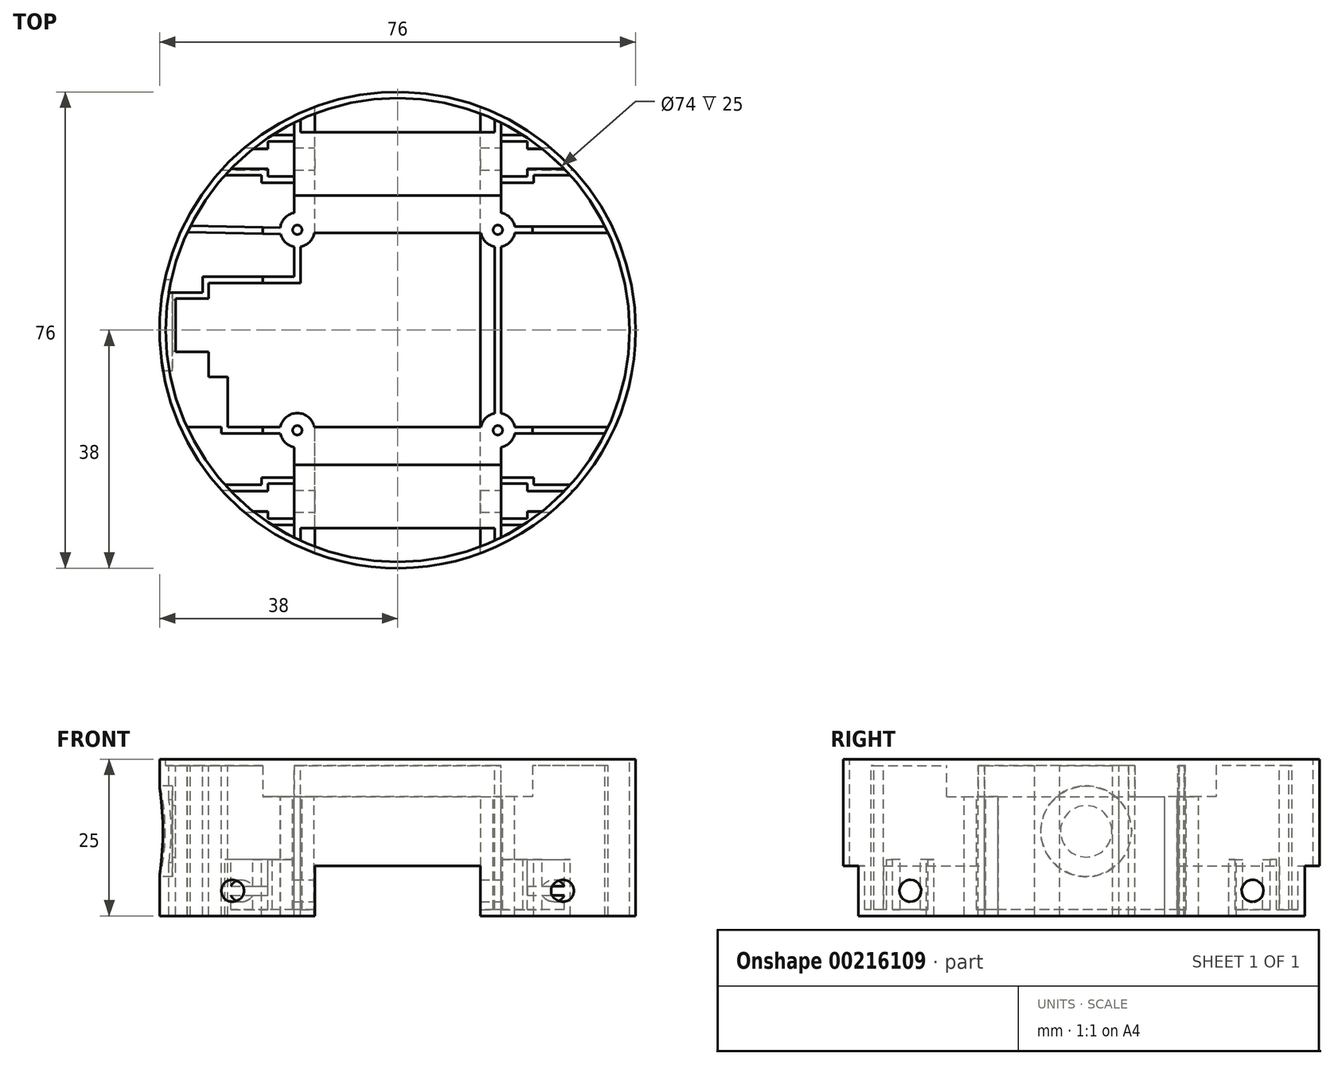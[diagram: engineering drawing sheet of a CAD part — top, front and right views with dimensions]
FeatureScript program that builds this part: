
annotation { "Feature Type Name" : "Feature", "Feature Type Description" : "" }
export const myFeature = defineFeature(function(context is Context, id is Id, definition is map)
    precondition{}
    {
        {
            var Q0;
            Q0=qCreatedBy(makeId("Top.planeOp"),FACE);
            var sketch = newSketch(context, id + "F0", { "sketchPlane" : qUnion([Q0])});
            skCircle(sketch, "E0", {"center": v(0, 0) * mm, "radius": 38 * mm});
            skLineSegment(sketch, "E1", {"start": v(-13, 35.7) * mm, "end": v(-13, -35.7) * mm, "construction": true});
            skLineSegment(sketch, "E2", {"start": v(13, 35.7) * mm, "end": v(13, -35.7) * mm, "construction": true});
            skLineSegment(sketch, "E3", {"start": v(0, 38) * mm, "end": v(0, -38) * mm, "construction": true});
            skSolve(sketch);
        }
        {
            var Q0;
            Q0=makeQuery(id+"F0.imprint","IMPRINT",FACE,{"disambiguationData":[TD([[makeQuery(id+"F0.imprint","IMPRINT",EDGE,{"derivedFrom":sQuery(id+"F0.wireOp",EDGE,"E0")}),1.0]])]});
            extrude(context, id + "F1", {"entities" : qUnion([Q0]), "depth" : 25 * mm});
        }
        {
            var Q0;
            Q0=makeQuery(id+"F1.opExtrude","CAP_FACE",FACE,{"disambiguationData":[OSD([sQuery(id+"F0.wireOp",EDGE,"E0")])],"isStart":false});
            var sketch = newSketch(context, id + "F2", { "sketchPlane" : qUnion([Q0])});
            skCircle(sketch, "E4", {"center": v(0, 0) * mm, "radius": 37 * mm});
            skLineSegment(sketch, "E5", {"start": v(-36.66, 5) * mm, "end": v(-30.14, 5) * mm});
            skLineSegment(sketch, "E6", {"start": v(-30.14, 5) * mm, "end": v(-30.14, 7.5) * mm});
            skLineSegment(sketch, "E7", {"start": v(-30.14, 7.5) * mm, "end": v(-27.14, 7.5) * mm});
            skLineSegment(sketch, "E8", {"start": v(-27.14, -7.5) * mm, "end": v(-30.14, -7.5) * mm});
            skLineSegment(sketch, "E9", {"start": v(-30.14, -7.5) * mm, "end": v(-30.14, -3.5) * mm});
            skLineSegment(sketch, "E10", {"start": v(-30.14, -3.5) * mm, "end": v(-36.83, -3.5) * mm});
            skLineSegment(sketch, "E11", {"start": v(0, 0) * mm, "end": v(-9.8, 0) * mm, "construction": true});
            skLineSegment(sketch, "E12", {"start": v(-27.14, -7.5) * mm, "end": v(-27.14, -15.5) * mm});
            skLineSegment(sketch, "E13", {"start": v(-35.44, 5) * mm, "end": v(-35.44, -3.5) * mm});
            skLineSegment(sketch, "E14", {"start": v(-36.51, 6) * mm, "end": v(-31.14, 6) * mm});
            skLineSegment(sketch, "E15", {"start": v(-31.14, 6) * mm, "end": v(-31.14, 8.5) * mm});
            skLineSegment(sketch, "E16", {"start": v(-31.14, 8.5) * mm, "end": v(-16.5, 8.5) * mm});
            skLineSegment(sketch, "E17", {"start": v(-21.04, -16.5) * mm, "end": v(-28.14, -16.5) * mm});
            skLineSegment(sketch, "E18", {"start": v(-28.14, -16.5) * mm, "end": v(-28.14, -8.5) * mm});
            skLineSegment(sketch, "E19", {"start": v(-28.14, -8.5) * mm, "end": v(-31.14, -8.5) * mm});
            skLineSegment(sketch, "E20", {"start": v(-31.14, -8.5) * mm, "end": v(-31.14, -4.5) * mm});
            skLineSegment(sketch, "E21", {"start": v(-31.14, -4.5) * mm, "end": v(-36.73, -4.5) * mm});
            skLineSegment(sketch, "E22", {"start": v(-33.49, -3.5) * mm, "end": v(-33.49, -4.5) * mm, "construction": true});
            skLineSegment(sketch, "E23", {"start": v(-30.14, -5.17) * mm, "end": v(-31.14, -5.17) * mm, "construction": true});
            skLineSegment(sketch, "E24", {"start": v(-29.18, -7.5) * mm, "end": v(-29.18, -8.5) * mm, "construction": true});
            skLineSegment(sketch, "E25", {"start": v(-28.14, -9.88) * mm, "end": v(-27.14, -9.88) * mm, "construction": true});
            skLineSegment(sketch, "E26", {"start": v(-23.9, -15.5) * mm, "end": v(-23.9, -16.5) * mm, "construction": true});
            skLineSegment(sketch, "E27", {"start": v(-9.14, -7.14) * mm, "end": v(-8.14, -7.14) * mm, "construction": true});
            skLineSegment(sketch, "E28", {"start": v(-20.62, 8.5) * mm, "end": v(-20.62, 7.5) * mm, "construction": true});
            skLineSegment(sketch, "E29", {"start": v(-32.73, 6) * mm, "end": v(-32.73, 5) * mm, "construction": true});
            skLineSegment(sketch, "E30", {"start": v(-31.14, 6.96) * mm, "end": v(-30.14, 6.96) * mm, "construction": true});
            skLineSegment(sketch, "E31.bottom", {"start": v(-16, 16) * mm, "end": v(16, 16) * mm, "construction": true});
            skLineSegment(sketch, "E31.top", {"start": v(-16, -16) * mm, "end": v(16, -16) * mm, "construction": true});
            skLineSegment(sketch, "E31.left", {"start": v(-16, 16) * mm, "end": v(-16, -16) * mm, "construction": true});
            skLineSegment(sketch, "E31.right", {"start": v(16, 16) * mm, "end": v(16, -16) * mm, "construction": true});
            skLineSegment(sketch, "E32", {"start": v(0, 0) * mm, "end": v(0, 2.04) * mm, "construction": true});
            skCircle(sketch, "E33", {"center": v(-16, 16) * mm, "radius": 0.75 * mm});
            skCircle(sketch, "E34", {"center": v(16, 16) * mm, "radius": 0.75 * mm});
            skCircle(sketch, "E35", {"center": v(16, -16) * mm, "radius": 0.75 * mm});
            skCircle(sketch, "E36", {"center": v(-16, -16) * mm, "radius": 0.75 * mm});
            skCircle(sketch, "E37", {"center": v(-16, 16) * mm, "radius": 2.75 * mm});
            skCircle(sketch, "E38", {"center": v(16, 16) * mm, "radius": 2.75 * mm});
            skCircle(sketch, "E39", {"center": v(-16, -16) * mm, "radius": 2.75 * mm});
            skCircle(sketch, "E40", {"center": v(16, -16) * mm, "radius": 2.75 * mm});
            skLineSegment(sketch, "E41", {"start": v(-16, 16.75) * mm, "end": v(-16, 18.75) * mm, "construction": true});
            skLineSegment(sketch, "E42", {"start": v(-16.5, 18.7) * mm, "end": v(-16.5, 33.12) * mm});
            skLineSegment(sketch, "E43", {"start": v(-16.5, 33.12) * mm, "end": v(-15.5, 33.6) * mm});
            skLineSegment(sketch, "E44", {"start": v(-15.5, 33.6) * mm, "end": v(-15.5, 18.7) * mm});
            skLineSegment(sketch, "E45", {"start": v(15.5, 18.7) * mm, "end": v(15.5, 33.6) * mm});
            skLineSegment(sketch, "E46", {"start": v(16.5, 18.7) * mm, "end": v(16.5, 33.12) * mm});
            skLineSegment(sketch, "E47", {"start": v(-18.73, 16.34) * mm, "end": v(-33.05, 16.63) * mm});
            skLineSegment(sketch, "E48", {"start": v(-18.67, 15.34) * mm, "end": v(-33.53, 15.63) * mm});
            skLineSegment(sketch, "E49", {"start": v(18.7, 16.5) * mm, "end": v(33.12, 16.5) * mm});
            skLineSegment(sketch, "E50", {"start": v(18.7, 15.5) * mm, "end": v(33.6, 15.5) * mm});
            skLineSegment(sketch, "E51", {"start": v(-18.7, -16.5) * mm, "end": v(-33.12, -16.5) * mm});
            skLineSegment(sketch, "E52", {"start": v(-18.7, -15.5) * mm, "end": v(-33.6, -15.5) * mm});
            skLineSegment(sketch, "E53", {"start": v(-16.5, -18.7) * mm, "end": v(-16.5, -33.12) * mm});
            skLineSegment(sketch, "E54", {"start": v(-15.5, -18.7) * mm, "end": v(-15.5, -33.6) * mm});
            skLineSegment(sketch, "E55", {"start": v(15.5, -18.7) * mm, "end": v(15.5, -33.6) * mm});
            skLineSegment(sketch, "E56", {"start": v(16.5, -18.7) * mm, "end": v(16.5, -33.12) * mm});
            skLineSegment(sketch, "E57", {"start": v(18.7, -15.5) * mm, "end": v(33.6, -15.5) * mm});
            skLineSegment(sketch, "E58", {"start": v(18.7, -16.5) * mm, "end": v(33.12, -16.5) * mm});
            skLineSegment(sketch, "E59", {"start": v(-13.3, 16.5) * mm, "end": v(13.3, 16.5) * mm});
            skLineSegment(sketch, "E60", {"start": v(-13.3, 15.5) * mm, "end": v(13.3, 15.5) * mm});
            skLineSegment(sketch, "E61", {"start": v(-16.5, 13.3) * mm, "end": v(-16.5, 8.5) * mm});
            skLineSegment(sketch, "E62", {"start": v(-15.5, 13.3) * mm, "end": v(-15.5, 8.5) * mm});
            skLineSegment(sketch, "E63", {"start": v(15.5, 13.3) * mm, "end": v(15.5, -13.3) * mm});
            skLineSegment(sketch, "E64", {"start": v(16.5, 13.3) * mm, "end": v(16.5, -13.3) * mm});
            skLineSegment(sketch, "E65", {"start": v(-13.3, -15.5) * mm, "end": v(13.3, -15.5) * mm});
            skLineSegment(sketch, "E66", {"start": v(-13.3, -16.5) * mm, "end": v(13.3, -16.5) * mm});
            skLineSegment(sketch, "E67", {"start": v(-25.45, -15.5) * mm, "end": v(-25.45, -16.5) * mm, "construction": true});
            skLineSegment(sketch, "E68", {"start": v(-16.5, -22.64) * mm, "end": v(-15.5, -22.64) * mm, "construction": true});
            skLineSegment(sketch, "E69", {"start": v(5.35, -15.5) * mm, "end": v(5.35, -16.5) * mm, "construction": true});
            skLineSegment(sketch, "E70", {"start": v(15.5, -24.3) * mm, "end": v(16.5, -24.3) * mm, "construction": true});
            skLineSegment(sketch, "E71", {"start": v(23.19, -15.5) * mm, "end": v(23.19, -16.5) * mm, "construction": true});
            skLineSegment(sketch, "E72", {"start": v(15.5, -9.1) * mm, "end": v(16.5, -9.1) * mm, "construction": true});
            skLineSegment(sketch, "E73", {"start": v(27.17, 16.5) * mm, "end": v(27.17, 15.5) * mm, "construction": true});
            skLineSegment(sketch, "E74", {"start": v(15.5, 26.6) * mm, "end": v(16.5, 26.6) * mm, "construction": true});
            skLineSegment(sketch, "E75", {"start": v(-15.5, 26.15) * mm, "end": v(-16.5, 26.15) * mm, "construction": true});
            skLineSegment(sketch, "E76", {"start": v(-25.9, 16.48) * mm, "end": v(-25.91, 15.48) * mm, "construction": true});
            skLineSegment(sketch, "E77", {"start": v(-15.5, 10.06) * mm, "end": v(-16.5, 10.06) * mm, "construction": true});
            skLineSegment(sketch, "E78", {"start": v(-3.42, 16.5) * mm, "end": v(-3.42, 15.5) * mm, "construction": true});
            skLineSegment(sketch, "E79.bottom", {"start": v(-16.5, 30.12) * mm, "end": v(-20.7, 30.12) * mm});
            skLineSegment(sketch, "E79.top", {"start": v(-16.5, 24.52) * mm, "end": v(-20.7, 24.52) * mm});
            skLineSegment(sketch, "E79.left", {"start": v(-16.5, 30.12) * mm, "end": v(-16.5, 24.52) * mm});
            skLineSegment(sketch, "E79.right", {"start": v(-20.7, 30.12) * mm, "end": v(-20.7, 24.52) * mm});
            skLineSegment(sketch, "E80", {"start": v(-20.7, 28.92) * mm, "end": v(-23.08, 28.92) * mm});
            skLineSegment(sketch, "E81", {"start": v(-26.6, 25.72) * mm, "end": v(-20.7, 25.72) * mm});
            skLineSegment(sketch, "E82", {"start": v(-16.5, 27.32) * mm, "end": v(-24.96, 27.32) * mm, "construction": true});
            skLineSegment(sketch, "E83", {"start": v(-16.5, 31.12) * mm, "end": v(-20.02, 31.12) * mm});
            skLineSegment(sketch, "E84", {"start": v(-27.53, 24.72) * mm, "end": v(-21.7, 24.72) * mm});
            skLineSegment(sketch, "E85", {"start": v(-21.7, 24.72) * mm, "end": v(-21.7, 23.52) * mm});
            skLineSegment(sketch, "E86", {"start": v(-21.7, 23.52) * mm, "end": v(-16.5, 23.52) * mm});
            skLineSegment(sketch, "E87", {"start": v(-18.26, 31.12) * mm, "end": v(-18.26, 30.12) * mm, "construction": true});
            skLineSegment(sketch, "E88", {"start": v(-25.05, 24.72) * mm, "end": v(-25.05, 25.72) * mm, "construction": true});
            skLineSegment(sketch, "E89", {"start": v(-21.7, 24.52) * mm, "end": v(-20.7, 24.52) * mm, "construction": true});
            skLineSegment(sketch, "E90", {"start": v(-17.39, 24.52) * mm, "end": v(-17.39, 23.52) * mm, "construction": true});
            skPoint(sketch, "E90.endSnap0", {"position": v(-19.1, 23.52) * mm});
            skLineSegment(sketch, "E91.MirrorCS", {"start": v(16.5, 31.12) * mm, "end": v(20.02, 31.12) * mm});
            skLineSegment(sketch, "E92.MirrorCS", {"start": v(16.5, 30.12) * mm, "end": v(20.7, 30.12) * mm});
            skLineSegment(sketch, "E93.MirrorCS", {"start": v(20.7, 28.92) * mm, "end": v(23.08, 28.92) * mm});
            skLineSegment(sketch, "E94.MirrorCS", {"start": v(20.7, 30.12) * mm, "end": v(20.7, 24.52) * mm});
            skLineSegment(sketch, "E95.MirrorCS", {"start": v(16.5, 24.52) * mm, "end": v(20.7, 24.52) * mm});
            skLineSegment(sketch, "E96.MirrorCS", {"start": v(21.7, 23.52) * mm, "end": v(16.5, 23.52) * mm});
            skLineSegment(sketch, "E97.MirrorCS", {"start": v(21.7, 24.72) * mm, "end": v(21.7, 23.52) * mm});
            skLineSegment(sketch, "E98.MirrorCS", {"start": v(27.53, 24.72) * mm, "end": v(21.7, 24.72) * mm});
            skLineSegment(sketch, "E99.MirrorCS", {"start": v(26.6, 25.72) * mm, "end": v(20.7, 25.72) * mm});
            skLineSegment(sketch, "E100.MirrorCS", {"start": v(-16.5, -30.12) * mm, "end": v(-20.7, -30.12) * mm});
            skLineSegment(sketch, "E101.MirrorCS", {"start": v(-16.5, -31.12) * mm, "end": v(-20.02, -31.12) * mm});
            skLineSegment(sketch, "E102.MirrorCS", {"start": v(-20.7, -28.92) * mm, "end": v(-23.08, -28.92) * mm});
            skLineSegment(sketch, "E103.MirrorCS", {"start": v(-26.6, -25.72) * mm, "end": v(-20.7, -25.72) * mm});
            skLineSegment(sketch, "E104.MirrorCS", {"start": v(-20.7, -30.12) * mm, "end": v(-20.7, -24.52) * mm});
            skLineSegment(sketch, "E105.MirrorCS", {"start": v(-16.5, -24.52) * mm, "end": v(-20.7, -24.52) * mm});
            skLineSegment(sketch, "E106.MirrorCS", {"start": v(-21.7, -24.72) * mm, "end": v(-21.7, -23.52) * mm});
            skLineSegment(sketch, "E107.MirrorCS", {"start": v(-27.53, -24.72) * mm, "end": v(-21.7, -24.72) * mm});
            skLineSegment(sketch, "E108.MirrorCS", {"start": v(-21.7, -23.52) * mm, "end": v(-16.5, -23.52) * mm});
            skLineSegment(sketch, "E109.MirrorCS", {"start": v(20.7, -28.92) * mm, "end": v(23.08, -28.92) * mm});
            skLineSegment(sketch, "E110.MirrorCS", {"start": v(16.5, -31.12) * mm, "end": v(20.02, -31.12) * mm});
            skLineSegment(sketch, "E111.MirrorCS", {"start": v(16.5, -30.12) * mm, "end": v(20.7, -30.12) * mm});
            skLineSegment(sketch, "E112.MirrorCS", {"start": v(21.7, -24.72) * mm, "end": v(21.7, -23.52) * mm});
            skLineSegment(sketch, "E113.MirrorCS", {"start": v(27.53, -24.72) * mm, "end": v(21.7, -24.72) * mm});
            skLineSegment(sketch, "E114.MirrorCS", {"start": v(26.6, -25.72) * mm, "end": v(20.7, -25.72) * mm});
            skLineSegment(sketch, "E115.MirrorCS", {"start": v(20.7, -30.12) * mm, "end": v(20.7, -24.52) * mm});
            skLineSegment(sketch, "E116.MirrorCS", {"start": v(16.5, -24.52) * mm, "end": v(20.7, -24.52) * mm});
            skLineSegment(sketch, "E117.MirrorCS", {"start": v(21.7, -23.52) * mm, "end": v(16.5, -23.52) * mm});
            skLineSegment(sketch, "E118.bottom", {"start": v(-15.5, 33.6) * mm, "end": v(15.5, 33.6) * mm});
            skLineSegment(sketch, "E118.top", {"start": v(-15.5, 31.6) * mm, "end": v(15.5, 31.6) * mm});
            skLineSegment(sketch, "E118.left", {"start": v(-15.5, 33.6) * mm, "end": v(-15.5, 31.6) * mm});
            skLineSegment(sketch, "E118.right", {"start": v(15.5, 33.6) * mm, "end": v(15.5, 31.6) * mm});
            skLineSegment(sketch, "E119.bottom", {"start": v(-15.5, -33.6) * mm, "end": v(15.5, -33.6) * mm});
            skLineSegment(sketch, "E119.top", {"start": v(-15.5, -31.6) * mm, "end": v(15.5, -31.6) * mm});
            skLineSegment(sketch, "E119.left", {"start": v(-15.5, -33.6) * mm, "end": v(-15.5, -31.6) * mm});
            skLineSegment(sketch, "E119.right", {"start": v(15.5, -33.6) * mm, "end": v(15.5, -31.6) * mm});
            skLineSegment(sketch, "E120", {"start": v(-0.86, -31.6) * mm, "end": v(-0.86, -33.6) * mm, "construction": true});
            skLineSegment(sketch, "E121", {"start": v(0, 33.6) * mm, "end": v(0, 31.6) * mm, "construction": true});
            skLineSegment(sketch, "E122", {"start": v(-30.14, 7.5) * mm, "end": v(-15.5, 7.5) * mm});
            skLineSegment(sketch, "E123", {"start": v(-15.5, 7.5) * mm, "end": v(-15.5, 8.5) * mm});
            skSolve(sketch);
        }
        {
            var Q0;
            {var subQ3=sQuery(id+"F2.wireOp",EDGE,"E6");Q0=makeQuery(id+"F2.imprint","IMPRINT",FACE,{"disambiguationData":[TD([[makeQuery(id+"F2.imprint","IMPRINT",EDGE,{"derivedFrom":subQ3}),-1.0]])]});}
            var Q1;
            {var subQ6=sQuery(id+"F2.wireOp",EDGE,"E14");Q1=makeQuery(id+"F2.imprint","IMPRINT",FACE,{"disambiguationData":[TD([[makeQuery(id+"F2.imprint","IMPRINT",EDGE,{"derivedFrom":subQ6}),1.0]])]});}
            var Q2;
            Q2=makeQuery(id+"F2.imprint","IMPRINT",FACE,{"disambiguationData":[TD([[makeQuery(id+"F2.imprint","IMPRINT",EDGE,{"derivedFrom":sQuery(id+"F2.wireOp",EDGE,"E35")}),1.0]])]});
            var Q3;
            Q3=makeQuery(id+"F2.imprint","IMPRINT",FACE,{"disambiguationData":[TD([[makeQuery(id+"F2.imprint","IMPRINT",EDGE,{"derivedFrom":sQuery(id+"F2.wireOp",EDGE,"E36")}),1.0]])]});
            var Q4;
            Q4=makeQuery(id+"F2.imprint","IMPRINT",FACE,{"disambiguationData":[TD([[makeQuery(id+"F2.imprint","IMPRINT",EDGE,{"derivedFrom":sQuery(id+"F2.wireOp",EDGE,"E34")}),1.0]])]});
            var Q5;
            Q5=makeQuery(id+"F2.imprint","IMPRINT",FACE,{"disambiguationData":[TD([[makeQuery(id+"F2.imprint","IMPRINT",EDGE,{"derivedFrom":sQuery(id+"F2.wireOp",EDGE,"E33")}),1.0]])]});
            var Q6;
            {var subQ0=sQuery(id+"F2.wireOp",EDGE,"E42");Q6=makeQuery(id+"F2.imprint","IMPRINT",FACE,{"disambiguationData":[TD([[makeQuery(id+"F2.imprint","IMPRINT",EDGE,{"derivedFrom":subQ0}),1.0]])]});}
            var Q7;
            {var subQ0=sQuery(id+"F2.wireOp",EDGE,"E44");Q7=makeQuery(id+"F2.imprint","IMPRINT",FACE,{"disambiguationData":[TD([[makeQuery(id+"F2.imprint","IMPRINT",EDGE,{"derivedFrom":subQ0}),1.0]])]});}
            var Q8;
            {var subQ9=sQuery(id+"F2.wireOp",EDGE,"0EzCJjks-PK91-1gbw-BSTb-mfvt5ydPBcno");Q8=makeQuery(id+"F2.imprint","IMPRINT",FACE,{"disambiguationData":[TD([[makeQuery(id+"F2.imprint","IMPRINT",EDGE,{"derivedFrom":subQ9}),1.0]])]});}
            var Q9;
            {var subQ0=sQuery(id+"F2.wireOp",EDGE,"E50");Q9=makeQuery(id+"F2.imprint","IMPRINT",FACE,{"disambiguationData":[TD([[makeQuery(id+"F2.imprint","IMPRINT",EDGE,{"derivedFrom":subQ0}),-1.0]])]});}
            var Q10;
            {var subQ0=sQuery(id+"F2.wireOp",EDGE,"E46");Q10=makeQuery(id+"F2.imprint","IMPRINT",FACE,{"disambiguationData":[TD([[makeQuery(id+"F2.imprint","IMPRINT",EDGE,{"derivedFrom":subQ0}),-1.0]])]});}
            var Q11;
            {var subQ0=sQuery(id+"F2.wireOp",EDGE,"E56");Q11=makeQuery(id+"F2.imprint","IMPRINT",FACE,{"disambiguationData":[TD([[makeQuery(id+"F2.imprint","IMPRINT",EDGE,{"derivedFrom":subQ0}),1.0]])]});}
            var Q12;
            {var subQ3=sQuery(id+"F2.wireOp",EDGE,"E54");Q12=makeQuery(id+"F2.imprint","IMPRINT",FACE,{"disambiguationData":[TD([[makeQuery(id+"F2.imprint","IMPRINT",EDGE,{"derivedFrom":subQ3}),1.0]])]});}
            var Q13;
            {var subQ0=sQuery(id+"F2.wireOp",EDGE,"E51");Q13=makeQuery(id+"F2.imprint","IMPRINT",FACE,{"disambiguationData":[TD([[makeQuery(id+"F2.imprint","IMPRINT",EDGE,{"derivedFrom":subQ0}),1.0]])]});}
            var Q14;
            {var subQ0=sQuery(id+"F2.wireOp",EDGE,"E18");Q14=makeQuery(id+"F2.imprint","IMPRINT",FACE,{"disambiguationData":[TD([[makeQuery(id+"F2.imprint","IMPRINT",EDGE,{"derivedFrom":subQ0}),1.0]])]});}
            var Q15;
            {var subQ3=sQuery(id+"F2.wireOp",EDGE,"E100.MirrorCS");Q15=makeQuery(id+"F2.imprint","IMPRINT",FACE,{"disambiguationData":[TD([[makeQuery(id+"F2.imprint","IMPRINT",EDGE,{"derivedFrom":subQ3}),-1.0]])]});}
            var Q16;
            {var subQ0=sQuery(id+"F2.wireOp",EDGE,"E102.MirrorCS");Q16=makeQuery(id+"F2.imprint","IMPRINT",FACE,{"disambiguationData":[TD([[makeQuery(id+"F2.imprint","IMPRINT",EDGE,{"derivedFrom":subQ0}),-1.0]])]});}
            var Q17;
            {var subQ3=sQuery(id+"F2.wireOp",EDGE,"E101.MirrorCS");Q17=makeQuery(id+"F2.imprint","IMPRINT",FACE,{"disambiguationData":[TD([[makeQuery(id+"F2.imprint","IMPRINT",EDGE,{"derivedFrom":subQ3}),1.0]])]});}
            var Q18;
            {var subQ2=sQuery(id+"F2.wireOp",EDGE,"E111.MirrorCS");Q18=makeQuery(id+"F2.imprint","IMPRINT",FACE,{"disambiguationData":[TD([[makeQuery(id+"F2.imprint","IMPRINT",EDGE,{"derivedFrom":subQ2}),1.0]])]});}
            var Q19;
            {var subQ0=sQuery(id+"F2.wireOp",EDGE,"E109.MirrorCS");Q19=makeQuery(id+"F2.imprint","IMPRINT",FACE,{"disambiguationData":[TD([[makeQuery(id+"F2.imprint","IMPRINT",EDGE,{"derivedFrom":subQ0}),1.0]])]});}
            var Q20;
            {var subQ0=sQuery(id+"F2.wireOp",EDGE,"E58");Q20=makeQuery(id+"F2.imprint","IMPRINT",FACE,{"disambiguationData":[TD([[makeQuery(id+"F2.imprint","IMPRINT",EDGE,{"derivedFrom":subQ0}),-1.0]])]});}
            var Q21;
            {var subQ0=sQuery(id+"F2.wireOp",EDGE,"E49");Q21=makeQuery(id+"F2.imprint","IMPRINT",FACE,{"disambiguationData":[TD([[makeQuery(id+"F2.imprint","IMPRINT",EDGE,{"derivedFrom":subQ0}),1.0]])]});}
            var Q22;
            {var subQ0=sQuery(id+"F2.wireOp",EDGE,"E93.MirrorCS");Q22=makeQuery(id+"F2.imprint","IMPRINT",FACE,{"disambiguationData":[TD([[makeQuery(id+"F2.imprint","IMPRINT",EDGE,{"derivedFrom":subQ0}),-1.0]])]});}
            var Q23;
            {var subQ3=sQuery(id+"F2.wireOp",EDGE,"E92.MirrorCS");Q23=makeQuery(id+"F2.imprint","IMPRINT",FACE,{"disambiguationData":[TD([[makeQuery(id+"F2.imprint","IMPRINT",EDGE,{"derivedFrom":subQ3}),-1.0]])]});}
            var Q24;
            {var subQ0=sQuery(id+"F2.wireOp",EDGE,"E47");Q24=makeQuery(id+"F2.imprint","IMPRINT",FACE,{"disambiguationData":[TD([[makeQuery(id+"F2.imprint","IMPRINT",EDGE,{"derivedFrom":subQ0}),-1.0]])]});}
            var Q25;
            {var subQ0=sQuery(id+"F2.wireOp",EDGE,"E80");Q25=makeQuery(id+"F2.imprint","IMPRINT",FACE,{"disambiguationData":[TD([[makeQuery(id+"F2.imprint","IMPRINT",EDGE,{"derivedFrom":subQ0}),1.0]])]});}
            var Q26;
            {var subQ1=sQuery(id+"F2.wireOp",EDGE,"E79.bottom");Q26=makeQuery(id+"F2.imprint","IMPRINT",FACE,{"disambiguationData":[TD([[makeQuery(id+"F2.imprint","IMPRINT",EDGE,{"derivedFrom":subQ1}),1.0]])]});}
            var Q27;
            {var subQ0=sQuery(id+"F2.wireOp",EDGE,"E119.bottom");Q27=makeQuery(id+"F2.imprint","IMPRINT",FACE,{"disambiguationData":[TD([[makeQuery(id+"F2.imprint","IMPRINT",EDGE,{"derivedFrom":subQ0}),-1.0]])]});}
            var Q28;
            {var subQ0=sQuery(id+"F2.wireOp",EDGE,"E118.bottom");Q28=makeQuery(id+"F2.imprint","IMPRINT",FACE,{"disambiguationData":[TD([[makeQuery(id+"F2.imprint","IMPRINT",EDGE,{"derivedFrom":subQ0}),1.0]])]});}
            extrude(context, id + "F3", {"entities" : qUnion([Q0, Q1, Q2, Q3, Q4, Q5, Q6, Q7, Q8, Q9, Q10, Q11, Q12, Q13, Q14, Q15, Q16, Q17, Q18, Q19, Q20, Q21, Q22, Q23, Q24, Q25, Q26, Q27, Q28]), "operationType" : NewBodyOperationType.REMOVE, "oppositeDirection" : true, "depth" : 24 * mm});
        }
        {
            var Q0;
            Q0=makeQuery(id+"F1.opExtrude","CAP_FACE",FACE,{"disambiguationData":[OSD([sQuery(id+"F0.wireOp",EDGE,"E0")])],"isStart":true});
            var sketch = newSketch(context, id + "F4", { "sketchPlane" : qUnion([Q0])});
            skLineSegment(sketch, "E124", {"start": v(-13.2, 35.63) * mm, "end": v(-13.2, -35.63) * mm});
            skLineSegment(sketch, "E125", {"start": v(13.2, 35.63) * mm, "end": v(13.2, -35.63) * mm});
            skLineSegment(sketch, "E126", {"start": v(0, 0) * mm, "end": v(0, 13.3) * mm, "construction": true});
            skSolve(sketch);
        }
        {
            var Q0;
            {var subQ0=sQuery(id+"F4.wireOp",EDGE,"E124");Q0=makeQuery(id+"F4.imprint","IMPRINT",FACE,{"disambiguationData":[TD([[makeQuery(id+"F4.imprint","IMPRINT",EDGE,{"derivedFrom":subQ0}),1.0]])]});}
            extrude(context, id + "F5", {"entities" : qUnion([Q0]), "operationType" : NewBodyOperationType.REMOVE, "oppositeDirection" : true, "depth" : 8 * mm});
        }
        {
            var Q0;
            Q0=makeQuery(id+"F1.opExtrude","CAP_FACE",FACE,{"disambiguationData":[OSD([sQuery(id+"F0.wireOp",EDGE,"E0")])],"isStart":false});
            var sketch = newSketch(context, id + "F6", { "sketchPlane" : qUnion([Q0])});
            skCircle(sketch, "E127", {"center": v(0, 0) * mm, "radius": 37 * mm});
            skSolve(sketch);
        }
        {
            var Q0;
            Q0 = qSketchRegion(id + "F6", true);
            extrude(context, id + "F7", {"entities" : qUnion([Q0]), "operationType" : NewBodyOperationType.REMOVE, "oppositeDirection" : true, "depth" : 1 * mm});
        }
        {
            var Q0;
            Q0=makeQuery(id+"F7.boolean.opBoolean","COPY",FACE,{"derivedFrom":makeQuery(id+"F7.opExtrude","CAP_FACE",FACE,{"disambiguationData":[OSD([sQuery(id+"F6.wireOp",EDGE,"E127")])],"isStart":false})});
            var sketch = newSketch(context, id + "F8", { "sketchPlane" : qUnion([Q0])});
            skLineSegment(sketch, "E128", {"start": v(0, 0) * mm, "end": v(0, 10.31) * mm, "construction": true});
            skLineSegment(sketch, "E129", {"start": v(0, 0) * mm, "end": v(0, 0) * mm});
            skLineSegment(sketch, "E130", {"start": v(0, 0) * mm, "end": v(9.54, 0) * mm, "construction": true});
            skLineSegment(sketch, "E131.bottom", {"start": v(-21.5, 21.5) * mm, "end": v(21.5, 21.5) * mm});
            skLineSegment(sketch, "E131.top", {"start": v(-21.5, -21.5) * mm, "end": v(21.5, -21.5) * mm});
            skLineSegment(sketch, "E131.left", {"start": v(-21.5, 21.5) * mm, "end": v(-21.5, -21.5) * mm});
            skLineSegment(sketch, "E131.right", {"start": v(21.5, 21.5) * mm, "end": v(21.5, -21.5) * mm});
            skSolve(sketch);
        }
        {
            var Q0;
            Q0 = qSketchRegion(id + "F8", true);
            extrude(context, id + "F9", {"entities" : qUnion([Q0]), "operationType" : NewBodyOperationType.REMOVE, "oppositeDirection" : true, "depth" : 5 * mm});
        }
        {
            var Q0;
            {var subQ0=sQuery(id+"F2.wireOp",EDGE,"E46");Q0=makeQuery(id+"F3.boolean.opBoolean","COPY",FACE,{"derivedFrom":makeQuery(id+"F3.opExtrude","SWEPT_FACE",FACE,{"disambiguationData":[OSD([subQ0]),TDD([makeQuery(id+"F2.imprint","IMPRINT",EDGE,{"disambiguationData":[TD([[makeQuery(id+"F2.imprint","INTERSECT",VERTEX,{"derivedFrom":[subQ0,sQuery(id+"F2.wireOp",EDGE,"E92.MirrorCS")]}),1.0]])],"derivedFrom":subQ0})])]})});}
            var sketch = newSketch(context, id + "F10", { "sketchPlane" : qUnion([Q0])});
            skLineSegment(sketch, "E132", {"start": v(27.32, 1) * mm, "end": v(27.32, 4) * mm, "construction": true});
            skCircle(sketch, "E133", {"center": v(27.32, 4) * mm, "radius": 1.75 * mm});
            skSolve(sketch);
        }
        {
            var Q0;
            {var subQ0=sQuery(id+"F2.wireOp",EDGE,"E56");Q0=makeQuery(id+"F3.boolean.opBoolean","COPY",FACE,{"derivedFrom":makeQuery(id+"F3.opExtrude","SWEPT_FACE",FACE,{"disambiguationData":[OSD([subQ0]),TDD([makeQuery(id+"F2.imprint","IMPRINT",EDGE,{"disambiguationData":[TD([[makeQuery(id+"F2.imprint","INTERSECT",VERTEX,{"derivedFrom":[subQ0,sQuery(id+"F2.wireOp",EDGE,"E111.MirrorCS")]}),1.0]])],"derivedFrom":subQ0})])]})});}
            var sketch = newSketch(context, id + "F11", { "sketchPlane" : qUnion([Q0])});
            skLineSegment(sketch, "E134", {"start": v(-27.32, 1) * mm, "end": v(-27.32, 4) * mm, "construction": true});
            skCircle(sketch, "E135", {"center": v(-27.32, 4) * mm, "radius": 1.75 * mm});
            skSolve(sketch);
        }
        {
            var Q0;
            Q0=makeQuery(id+"F10.imprint","IMPRINT",FACE,{"disambiguationData":[TD([[makeQuery(id+"F10.imprint","IMPRINT",EDGE,{"derivedFrom":sQuery(id+"F10.wireOp",EDGE,"E133")}),1.0]])]});
            var Q1;
            Q1=makeQuery(id+"F11.imprint","IMPRINT",FACE,{"disambiguationData":[TD([[makeQuery(id+"F11.imprint","IMPRINT",EDGE,{"derivedFrom":sQuery(id+"F11.wireOp",EDGE,"E135")}),1.0]])]});
            extrude(context, id + "F12", {"entities" : qUnion([Q0, Q1]), "operationType" : NewBodyOperationType.REMOVE, "endBound" : BoundingType.SYMMETRIC, "oppositeDirection" : true, "depth" : 100 * mm});
        }
        {
            var Q0;
            {var subQ24=sQuery(id+"F6.wireOp",EDGE,"E127");Q0=makeQuery(id+"F9.boolean.opBoolean","SPLIT",FACE,{"disambiguationData":[TD([makeQuery(id+"F3.boolean.opBoolean","COPY",FACE,{"derivedFrom":makeQuery(id+"F3.opExtrude","SWEPT_FACE",FACE,{"disambiguationData":[OSD([sQuery(id+"F2.wireOp",EDGE,"E44")])]})})])],"derivedFrom":makeQuery(id+"F7.boolean.opBoolean","COPY",FACE,{"derivedFrom":makeQuery(id+"F7.opExtrude","CAP_FACE",FACE,{"disambiguationData":[OSD([subQ24])],"isStart":false})})});}
            var sketch = newSketch(context, id + "F13", { "sketchPlane" : qUnion([Q0])});
            skCircle(sketch, "E136", {"center": v(0, 0) * mm, "radius": 37 * mm});
            skLineSegment(sketch, "E137", {"start": v(16.5, 33.12) * mm, "end": v(16.5, 23.52) * mm});
            skLineSegment(sketch, "E138", {"start": v(16.5, 23.52) * mm, "end": v(28.56, 23.52) * mm});
            skLineSegment(sketch, "E139", {"start": v(-16.5, 33.12) * mm, "end": v(-16.5, 23.52) * mm});
            skLineSegment(sketch, "E140", {"start": v(-16.5, 23.52) * mm, "end": v(-28.56, 23.52) * mm});
            skSolve(sketch);
        }
        {
            var Q0;
            {var subQ1=makeQuery(id+"F7.opExtrude","CAP_FACE",FACE,{"disambiguationData":[OSD([sQuery(id+"F6.wireOp",EDGE,"E127")])],"isStart":false});var subQ5=makeQuery(id+"F7.boolean.opBoolean","INTERSECT",EDGE,{"derivedFrom":[makeQuery(id+"F3.boolean.opBoolean","COPY",FACE,{"derivedFrom":makeQuery(id+"F3.opExtrude","SWEPT_FACE",FACE,{"disambiguationData":[OSD([sQuery(id+"F2.wireOp",EDGE,"E97.MirrorCS")])]})}),subQ1]});Q0=makeQuery(id+"F13.imprint","IMPRINT",FACE,{"disambiguationData":[TD([[makeQuery(id+"F13.imprint","IMPRINT",EDGE,{"derivedFrom":subQ5}),-1.0]])]});}
            var Q1;
            {var subQ3=makeQuery(id+"F7.boolean.opBoolean","INTERSECT",EDGE,{"derivedFrom":[makeQuery(id+"F3.boolean.opBoolean","COPY",FACE,{"derivedFrom":makeQuery(id+"F3.opExtrude","SWEPT_FACE",FACE,{"disambiguationData":[OSD([sQuery(id+"F2.wireOp",EDGE,"E91.MirrorCS")])]})}),makeQuery(id+"F7.opExtrude","CAP_FACE",FACE,{"disambiguationData":[OSD([sQuery(id+"F6.wireOp",EDGE,"E127")])],"isStart":false})]});Q1=makeQuery(id+"F13.imprint","IMPRINT",FACE,{"disambiguationData":[TD([[makeQuery(id+"F13.imprint","IMPRINT",EDGE,{"derivedFrom":subQ3}),-1.0]])]});}
            var Q2;
            {var subQ3=makeQuery(id+"F7.boolean.opBoolean","INTERSECT",EDGE,{"derivedFrom":[makeQuery(id+"F3.boolean.opBoolean","COPY",FACE,{"derivedFrom":makeQuery(id+"F3.opExtrude","SWEPT_FACE",FACE,{"disambiguationData":[OSD([sQuery(id+"F2.wireOp",EDGE,"E83")])]})}),makeQuery(id+"F7.opExtrude","CAP_FACE",FACE,{"disambiguationData":[OSD([sQuery(id+"F6.wireOp",EDGE,"E127")])],"isStart":false})]});Q2=makeQuery(id+"F13.imprint","IMPRINT",FACE,{"disambiguationData":[TD([[makeQuery(id+"F13.imprint","IMPRINT",EDGE,{"derivedFrom":subQ3}),1.0]])]});}
            var Q3;
            {var subQ1=makeQuery(id+"F7.opExtrude","CAP_FACE",FACE,{"disambiguationData":[OSD([sQuery(id+"F6.wireOp",EDGE,"E127")])],"isStart":false});var subQ2=makeQuery(id+"F7.boolean.opBoolean","INTERSECT",EDGE,{"derivedFrom":[makeQuery(id+"F3.boolean.opBoolean","COPY",FACE,{"derivedFrom":makeQuery(id+"F3.opExtrude","SWEPT_FACE",FACE,{"disambiguationData":[OSD([sQuery(id+"F2.wireOp",EDGE,"E84")])]})}),subQ1]});Q3=makeQuery(id+"F13.imprint","IMPRINT",FACE,{"disambiguationData":[TD([[makeQuery(id+"F13.imprint","IMPRINT",EDGE,{"derivedFrom":subQ2}),1.0]])]});}
            var Q4;
            {var subQ0=makeQuery(id+"F7.opExtrude","CAP_FACE",FACE,{"disambiguationData":[OSD([sQuery(id+"F6.wireOp",EDGE,"E127")])],"isStart":false});var subQ4=sQuery(id+"F2.wireOp",EDGE,"E92.MirrorCS");var subQ5=makeQuery(id+"F7.boolean.opBoolean","INTERSECT",EDGE,{"derivedFrom":[makeQuery(id+"F3.boolean.opBoolean","COPY",FACE,{"derivedFrom":makeQuery(id+"F3.opExtrude","SWEPT_FACE",FACE,{"disambiguationData":[OSD([subQ4])]})}),subQ0]});Q4=makeQuery(id+"F13.imprint","IMPRINT",FACE,{"disambiguationData":[TD([[makeQuery(id+"F13.imprint","IMPRINT",EDGE,{"derivedFrom":subQ5}),1.0]])]});}
            var Q5;
            {var subQ0=makeQuery(id+"F7.opExtrude","CAP_FACE",FACE,{"disambiguationData":[OSD([sQuery(id+"F6.wireOp",EDGE,"E127")])],"isStart":false});var subQ3=makeQuery(id+"F7.boolean.opBoolean","INTERSECT",EDGE,{"derivedFrom":[makeQuery(id+"F3.boolean.opBoolean","COPY",FACE,{"derivedFrom":makeQuery(id+"F3.opExtrude","SWEPT_FACE",FACE,{"disambiguationData":[OSD([sQuery(id+"F2.wireOp",EDGE,"E91.MirrorCS")])]})}),subQ0]});Q5=makeQuery(id+"F13.imprint","IMPRINT",FACE,{"disambiguationData":[TD([[makeQuery(id+"F13.imprint","IMPRINT",EDGE,{"derivedFrom":subQ3}),1.0]])]});}
            var Q6;
            {var subQ1=makeQuery(id+"F7.opExtrude","CAP_FACE",FACE,{"disambiguationData":[OSD([sQuery(id+"F6.wireOp",EDGE,"E127")])],"isStart":false});var subQ2=sQuery(id+"F2.wireOp",EDGE,"E79.bottom");var subQ3=makeQuery(id+"F7.boolean.opBoolean","INTERSECT",EDGE,{"derivedFrom":[makeQuery(id+"F3.boolean.opBoolean","COPY",FACE,{"derivedFrom":makeQuery(id+"F3.opExtrude","SWEPT_FACE",FACE,{"disambiguationData":[OSD([subQ2])]})}),subQ1]});Q6=makeQuery(id+"F13.imprint","IMPRINT",FACE,{"disambiguationData":[TD([[makeQuery(id+"F13.imprint","IMPRINT",EDGE,{"derivedFrom":subQ3}),1.0]])]});}
            var Q7;
            {var subQ0=makeQuery(id+"F7.opExtrude","CAP_FACE",FACE,{"disambiguationData":[OSD([sQuery(id+"F6.wireOp",EDGE,"E127")])],"isStart":false});var subQ5=sQuery(id+"F2.wireOp",EDGE,"E79.bottom");var subQ6=makeQuery(id+"F7.boolean.opBoolean","INTERSECT",EDGE,{"derivedFrom":[makeQuery(id+"F3.boolean.opBoolean","COPY",FACE,{"derivedFrom":makeQuery(id+"F3.opExtrude","SWEPT_FACE",FACE,{"disambiguationData":[OSD([subQ5])]})}),subQ0]});Q7=makeQuery(id+"F13.imprint","IMPRINT",FACE,{"disambiguationData":[TD([[makeQuery(id+"F13.imprint","IMPRINT",EDGE,{"derivedFrom":subQ6}),-1.0]])]});}
            var Q8;
            {var subQ0=makeQuery(id+"F7.opExtrude","CAP_FACE",FACE,{"disambiguationData":[OSD([sQuery(id+"F6.wireOp",EDGE,"E127")])],"isStart":false});var subQ1=sQuery(id+"F2.wireOp",EDGE,"E95.MirrorCS");var subQ9=makeQuery(id+"F7.boolean.opBoolean","INTERSECT",EDGE,{"derivedFrom":[makeQuery(id+"F3.boolean.opBoolean","COPY",FACE,{"derivedFrom":makeQuery(id+"F3.opExtrude","SWEPT_FACE",FACE,{"disambiguationData":[OSD([subQ1])]})}),subQ0]});Q8=makeQuery(id+"F13.imprint","IMPRINT",FACE,{"disambiguationData":[TD([[makeQuery(id+"F13.imprint","IMPRINT",EDGE,{"derivedFrom":subQ9}),1.0]])]});}
            var Q9;
            {var subQ0=makeQuery(id+"F7.opExtrude","CAP_FACE",FACE,{"disambiguationData":[OSD([sQuery(id+"F6.wireOp",EDGE,"E127")])],"isStart":false});var subQ1=sQuery(id+"F2.wireOp",EDGE,"E79.top");var subQ2=makeQuery(id+"F7.boolean.opBoolean","INTERSECT",EDGE,{"derivedFrom":[makeQuery(id+"F3.boolean.opBoolean","COPY",FACE,{"derivedFrom":makeQuery(id+"F3.opExtrude","SWEPT_FACE",FACE,{"disambiguationData":[OSD([subQ1])]})}),subQ0]});Q9=makeQuery(id+"F13.imprint","IMPRINT",FACE,{"disambiguationData":[TD([[makeQuery(id+"F13.imprint","IMPRINT",EDGE,{"derivedFrom":subQ2}),-1.0]])]});}
            extrude(context, id + "F14", {"entities" : qUnion([Q0, Q1, Q2, Q3, Q4, Q5, Q6, Q7, Q8, Q9]), "operationType" : NewBodyOperationType.REMOVE, "oppositeDirection" : true, "depth" : 15 * mm});
        }
        {
            var Q0;
            {var subQ20=sQuery(id+"F6.wireOp",EDGE,"E127");Q0=makeQuery(id+"F9.boolean.opBoolean","SPLIT",FACE,{"disambiguationData":[TD([makeQuery(id+"F3.boolean.opBoolean","COPY",FACE,{"derivedFrom":makeQuery(id+"F3.opExtrude","SWEPT_FACE",FACE,{"disambiguationData":[OSD([sQuery(id+"F2.wireOp",EDGE,"E54")])]})})])],"derivedFrom":makeQuery(id+"F7.boolean.opBoolean","COPY",FACE,{"derivedFrom":makeQuery(id+"F7.opExtrude","CAP_FACE",FACE,{"disambiguationData":[OSD([subQ20])],"isStart":false})})});}
            var sketch = newSketch(context, id + "F15", { "sketchPlane" : qUnion([Q0])});
            skCircle(sketch, "E141", {"center": v(0, 0) * mm, "radius": 37 * mm});
            skLineSegment(sketch, "E142", {"start": v(-16.5, -23.52) * mm, "end": v(-28.56, -23.52) * mm});
            skLineSegment(sketch, "E143", {"start": v(-16.5, -33.12) * mm, "end": v(-16.5, -23.52) * mm});
            skLineSegment(sketch, "E144", {"start": v(16.5, -33.12) * mm, "end": v(16.5, -23.52) * mm});
            skLineSegment(sketch, "E145", {"start": v(16.5, -23.52) * mm, "end": v(28.56, -23.52) * mm});
            skSolve(sketch);
        }
        {
            var Q0;
            {var subQ1=makeQuery(id+"F7.opExtrude","CAP_FACE",FACE,{"disambiguationData":[OSD([sQuery(id+"F6.wireOp",EDGE,"E127")])],"isStart":false});var subQ5=makeQuery(id+"F7.boolean.opBoolean","INTERSECT",EDGE,{"derivedFrom":[makeQuery(id+"F3.boolean.opBoolean","COPY",FACE,{"derivedFrom":makeQuery(id+"F3.opExtrude","SWEPT_FACE",FACE,{"disambiguationData":[OSD([sQuery(id+"F2.wireOp",EDGE,"E106.MirrorCS")])]})}),subQ1]});Q0=makeQuery(id+"F15.imprint","IMPRINT",FACE,{"disambiguationData":[TD([[makeQuery(id+"F15.imprint","IMPRINT",EDGE,{"derivedFrom":subQ5}),-1.0]])]});}
            var Q1;
            {var subQ3=makeQuery(id+"F7.boolean.opBoolean","INTERSECT",EDGE,{"derivedFrom":[makeQuery(id+"F3.boolean.opBoolean","COPY",FACE,{"derivedFrom":makeQuery(id+"F3.opExtrude","SWEPT_FACE",FACE,{"disambiguationData":[OSD([sQuery(id+"F2.wireOp",EDGE,"E101.MirrorCS")])]})}),makeQuery(id+"F7.opExtrude","CAP_FACE",FACE,{"disambiguationData":[OSD([sQuery(id+"F6.wireOp",EDGE,"E127")])],"isStart":false})]});Q1=makeQuery(id+"F15.imprint","IMPRINT",FACE,{"disambiguationData":[TD([[makeQuery(id+"F15.imprint","IMPRINT",EDGE,{"derivedFrom":subQ3}),-1.0]])]});}
            var Q2;
            {var subQ3=makeQuery(id+"F7.boolean.opBoolean","INTERSECT",EDGE,{"derivedFrom":[makeQuery(id+"F3.boolean.opBoolean","COPY",FACE,{"derivedFrom":makeQuery(id+"F3.opExtrude","SWEPT_FACE",FACE,{"disambiguationData":[OSD([sQuery(id+"F2.wireOp",EDGE,"E110.MirrorCS")])]})}),makeQuery(id+"F7.opExtrude","CAP_FACE",FACE,{"disambiguationData":[OSD([sQuery(id+"F6.wireOp",EDGE,"E127")])],"isStart":false})]});Q2=makeQuery(id+"F15.imprint","IMPRINT",FACE,{"disambiguationData":[TD([[makeQuery(id+"F15.imprint","IMPRINT",EDGE,{"derivedFrom":subQ3}),1.0]])]});}
            var Q3;
            {var subQ1=makeQuery(id+"F7.opExtrude","CAP_FACE",FACE,{"disambiguationData":[OSD([sQuery(id+"F6.wireOp",EDGE,"E127")])],"isStart":false});var subQ5=makeQuery(id+"F7.boolean.opBoolean","INTERSECT",EDGE,{"derivedFrom":[makeQuery(id+"F3.boolean.opBoolean","COPY",FACE,{"derivedFrom":makeQuery(id+"F3.opExtrude","SWEPT_FACE",FACE,{"disambiguationData":[OSD([sQuery(id+"F2.wireOp",EDGE,"E112.MirrorCS")])]})}),subQ1]});Q3=makeQuery(id+"F15.imprint","IMPRINT",FACE,{"disambiguationData":[TD([[makeQuery(id+"F15.imprint","IMPRINT",EDGE,{"derivedFrom":subQ5}),1.0]])]});}
            var Q4;
            {var subQ0=makeQuery(id+"F7.opExtrude","CAP_FACE",FACE,{"disambiguationData":[OSD([sQuery(id+"F6.wireOp",EDGE,"E127")])],"isStart":false});var subQ1=sQuery(id+"F2.wireOp",EDGE,"E100.MirrorCS");var subQ2=makeQuery(id+"F7.boolean.opBoolean","INTERSECT",EDGE,{"derivedFrom":[makeQuery(id+"F3.boolean.opBoolean","COPY",FACE,{"derivedFrom":makeQuery(id+"F3.opExtrude","SWEPT_FACE",FACE,{"disambiguationData":[OSD([subQ1])]})}),subQ0]});Q4=makeQuery(id+"F15.imprint","IMPRINT",FACE,{"disambiguationData":[TD([[makeQuery(id+"F15.imprint","IMPRINT",EDGE,{"derivedFrom":subQ2}),1.0]])]});}
            var Q5;
            {var subQ0=makeQuery(id+"F7.opExtrude","CAP_FACE",FACE,{"disambiguationData":[OSD([sQuery(id+"F6.wireOp",EDGE,"E127")])],"isStart":false});var subQ2=sQuery(id+"F2.wireOp",EDGE,"E100.MirrorCS");var subQ3=makeQuery(id+"F7.boolean.opBoolean","INTERSECT",EDGE,{"derivedFrom":[makeQuery(id+"F3.boolean.opBoolean","COPY",FACE,{"derivedFrom":makeQuery(id+"F3.opExtrude","SWEPT_FACE",FACE,{"disambiguationData":[OSD([subQ2])]})}),subQ0]});Q5=makeQuery(id+"F15.imprint","IMPRINT",FACE,{"disambiguationData":[TD([[makeQuery(id+"F15.imprint","IMPRINT",EDGE,{"derivedFrom":subQ3}),-1.0]])]});}
            var Q6;
            {var subQ0=makeQuery(id+"F7.opExtrude","CAP_FACE",FACE,{"disambiguationData":[OSD([sQuery(id+"F6.wireOp",EDGE,"E127")])],"isStart":false});var subQ1=sQuery(id+"F2.wireOp",EDGE,"E109.MirrorCS");var subQ2=makeQuery(id+"F7.boolean.opBoolean","INTERSECT",EDGE,{"derivedFrom":[makeQuery(id+"F3.boolean.opBoolean","COPY",FACE,{"derivedFrom":makeQuery(id+"F3.opExtrude","SWEPT_FACE",FACE,{"disambiguationData":[OSD([subQ1])]})}),subQ0]});Q6=makeQuery(id+"F15.imprint","IMPRINT",FACE,{"disambiguationData":[TD([[makeQuery(id+"F15.imprint","IMPRINT",EDGE,{"derivedFrom":subQ2}),1.0]])]});}
            var Q7;
            {var subQ0=makeQuery(id+"F7.opExtrude","CAP_FACE",FACE,{"disambiguationData":[OSD([sQuery(id+"F6.wireOp",EDGE,"E127")])],"isStart":false});var subQ3=sQuery(id+"F2.wireOp",EDGE,"E109.MirrorCS");var subQ4=makeQuery(id+"F7.boolean.opBoolean","INTERSECT",EDGE,{"derivedFrom":[makeQuery(id+"F3.boolean.opBoolean","COPY",FACE,{"derivedFrom":makeQuery(id+"F3.opExtrude","SWEPT_FACE",FACE,{"disambiguationData":[OSD([subQ3])]})}),subQ0]});Q7=makeQuery(id+"F15.imprint","IMPRINT",FACE,{"disambiguationData":[TD([[makeQuery(id+"F15.imprint","IMPRINT",EDGE,{"derivedFrom":subQ4}),-1.0]])]});}
            var Q8;
            {var subQ0=makeQuery(id+"F7.opExtrude","CAP_FACE",FACE,{"disambiguationData":[OSD([sQuery(id+"F6.wireOp",EDGE,"E127")])],"isStart":false});var subQ1=sQuery(id+"F2.wireOp",EDGE,"E103.MirrorCS");var subQ2=makeQuery(id+"F7.boolean.opBoolean","INTERSECT",EDGE,{"derivedFrom":[makeQuery(id+"F3.boolean.opBoolean","COPY",FACE,{"derivedFrom":makeQuery(id+"F3.opExtrude","SWEPT_FACE",FACE,{"disambiguationData":[OSD([subQ1])]})}),subQ0]});Q8=makeQuery(id+"F15.imprint","IMPRINT",FACE,{"disambiguationData":[TD([[makeQuery(id+"F15.imprint","IMPRINT",EDGE,{"derivedFrom":subQ2}),-1.0]])]});}
            var Q9;
            {var subQ0=makeQuery(id+"F7.opExtrude","CAP_FACE",FACE,{"disambiguationData":[OSD([sQuery(id+"F6.wireOp",EDGE,"E127")])],"isStart":false});var subQ1=makeQuery(id+"F7.boolean.opBoolean","INTERSECT",EDGE,{"derivedFrom":[makeQuery(id+"F3.boolean.opBoolean","COPY",FACE,{"derivedFrom":makeQuery(id+"F3.opExtrude","SWEPT_FACE",FACE,{"disambiguationData":[OSD([sQuery(id+"F2.wireOp",EDGE,"E112.MirrorCS")])]})}),subQ0]});Q9=makeQuery(id+"F15.imprint","IMPRINT",FACE,{"disambiguationData":[TD([[makeQuery(id+"F15.imprint","IMPRINT",EDGE,{"derivedFrom":subQ1}),-1.0]])]});}
            extrude(context, id + "F16", {"entities" : qUnion([Q0, Q1, Q2, Q3, Q4, Q5, Q6, Q7, Q8, Q9]), "operationType" : NewBodyOperationType.REMOVE, "oppositeDirection" : true, "depth" : 15 * mm});
        }
        {
            var Q0;
            Q0=makeQuery(id+"F3.boolean.opBoolean","COPY",FACE,{"derivedFrom":makeQuery(id+"F3.opExtrude","SWEPT_FACE",FACE,{"disambiguationData":[OSD([sQuery(id+"F2.wireOp",EDGE,"E13")])]})});
            var sketch = newSketch(context, id + "F17", { "sketchPlane" : qUnion([Q0])});
            skLineSegment(sketch, "E146", {"start": v(0.75, 24) * mm, "end": v(0.75, 1) * mm, "construction": true});
            skCircle(sketch, "E147", {"center": v(0.75, 13.5) * mm, "radius": 4.1 * mm});
            skSolve(sketch);
        }
        {
            var Q0;
            Q0=makeQuery(id+"F17.imprint","IMPRINT",FACE,{"disambiguationData":[TD([[makeQuery(id+"F17.imprint","IMPRINT",EDGE,{"derivedFrom":sQuery(id+"F17.wireOp",EDGE,"E147")}),1.0]])]});
            extrude(context, id + "F18", {"entities" : qUnion([Q0]), "operationType" : NewBodyOperationType.REMOVE, "oppositeDirection" : true, "depth" : 2.5 * mm});
        }
        {
            var Q0;
            Q0=makeQuery(id+"F18.boolean.opBoolean","COPY",FACE,{"derivedFrom":makeQuery(id+"F18.opExtrude","CAP_FACE",FACE,{"disambiguationData":[OSD([sQuery(id+"F17.wireOp",EDGE,"E147")])],"isStart":false})});
            var sketch = newSketch(context, id + "F19", { "sketchPlane" : qUnion([Q0])});
            skCircle(sketch, "E148", {"center": v(0.75, 13.5) * mm, "radius": 7.25 * mm});
            skLineSegment(sketch, "E149", {"start": v(0, 11) * mm, "end": v(0, 16) * mm, "construction": true});
            skSolve(sketch);
        }
        {
            var Q0;
            Q0=makeQuery(id+"F19.imprint","IMPRINT",FACE,{"disambiguationData":[TD([[makeQuery(id+"F19.imprint","IMPRINT",EDGE,{"derivedFrom":sQuery(id+"F19.wireOp",EDGE,"E148")}),1.0]])]});
            extrude(context, id + "F20", {"entities" : qUnion([Q0]), "operationType" : NewBodyOperationType.REMOVE, "endBound" : BoundingType.SYMMETRIC, "offsetDistance" : 25 * mm, "depth" : 4 * mm});
        }
        {
            var Q0;
            Q0=makeQuery(id+"F18.boolean.opBoolean","COPY",FACE,{"derivedFrom":makeQuery(id+"F18.opExtrude","CAP_FACE",FACE,{"disambiguationData":[OSD([sQuery(id+"F17.wireOp",EDGE,"E147")])],"isStart":false})});
            extrude(context, id + "F21", {"entities" : qUnion([Q0]), "operationType" : NewBodyOperationType.REMOVE, "oppositeDirection" : true, "depth" : 25 * mm});
        }
        {
            var Q0;
            Q0=makeQuery(id+"F3.boolean.opBoolean","COPY",FACE,{"derivedFrom":makeQuery(id+"F3.opExtrude","CAP_FACE",FACE,{"disambiguationData":[OSD([sQuery(id+"F2.wireOp",EDGE,"E4"),sQuery(id+"F2.wireOp",EDGE,"E38"),sQuery(id+"F2.wireOp",EDGE,"E40"),sQuery(id+"F2.wireOp",EDGE,"E50"),sQuery(id+"F2.wireOp",EDGE,"E57"),sQuery(id+"F2.wireOp",EDGE,"E64")])],"isStart":false})});
            var Q1;
            Q1=makeQuery(id+"F3.boolean.opBoolean","COPY",FACE,{"derivedFrom":makeQuery(id+"F3.opExtrude","CAP_FACE",FACE,{"disambiguationData":[OSD([sQuery(id+"F2.wireOp",EDGE,"E4"),sQuery(id+"F2.wireOp",EDGE,"E40"),sQuery(id+"F2.wireOp",EDGE,"E56"),sQuery(id+"F2.wireOp",EDGE,"E58"),sQuery(id+"F2.wireOp",EDGE,"E112.MirrorCS"),sQuery(id+"F2.wireOp",EDGE,"E113.MirrorCS"),sQuery(id+"F2.wireOp",EDGE,"E117.MirrorCS")])],"isStart":false})});
            var Q2;
            Q2=makeQuery(id+"F3.boolean.opBoolean","COPY",FACE,{"derivedFrom":makeQuery(id+"F3.opExtrude","CAP_FACE",FACE,{"disambiguationData":[OSD([sQuery(id+"F2.wireOp",EDGE,"E4"),sQuery(id+"F2.wireOp",EDGE,"E38"),sQuery(id+"F2.wireOp",EDGE,"E46"),sQuery(id+"F2.wireOp",EDGE,"E49"),sQuery(id+"F2.wireOp",EDGE,"E96.MirrorCS"),sQuery(id+"F2.wireOp",EDGE,"E97.MirrorCS"),sQuery(id+"F2.wireOp",EDGE,"E98.MirrorCS")])],"isStart":false})});
            var Q3;
            Q3=makeQuery(id+"F3.boolean.opBoolean","COPY",FACE,{"derivedFrom":makeQuery(id+"F3.opExtrude","CAP_FACE",FACE,{"disambiguationData":[OSD([sQuery(id+"F2.wireOp",EDGE,"E4"),sQuery(id+"F2.wireOp",EDGE,"E37"),sQuery(id+"F2.wireOp",EDGE,"E42"),sQuery(id+"F2.wireOp",EDGE,"E47"),sQuery(id+"F2.wireOp",EDGE,"E84"),sQuery(id+"F2.wireOp",EDGE,"E85"),sQuery(id+"F2.wireOp",EDGE,"E86")])],"isStart":false})});
            var Q4;
            Q4=makeQuery(id+"F3.boolean.opBoolean","COPY",FACE,{"derivedFrom":makeQuery(id+"F3.opExtrude","CAP_FACE",FACE,{"disambiguationData":[OSD([sQuery(id+"F2.wireOp",EDGE,"E4"),sQuery(id+"F2.wireOp",EDGE,"E14"),sQuery(id+"F2.wireOp",EDGE,"E15"),sQuery(id+"F2.wireOp",EDGE,"E16"),sQuery(id+"F2.wireOp",EDGE,"E37"),sQuery(id+"F2.wireOp",EDGE,"E48"),sQuery(id+"F2.wireOp",EDGE,"E61")])],"isStart":false})});
            var Q5;
            {var subQ0=sQuery(id+"F2.wireOp",EDGE,"E52");var subQ1=sQuery(id+"F2.wireOp",EDGE,"E39");var subQ3=sQuery(id+"F2.wireOp",EDGE,"E65");var subQ4=sQuery(id+"F2.wireOp",EDGE,"E12");var subQ5=sQuery(id+"F2.wireOp",EDGE,"E13");var subQ6=sQuery(id+"F2.wireOp",EDGE,"E8");var subQ7=sQuery(id+"F2.wireOp",EDGE,"E10");var subQ8=sQuery(id+"F2.wireOp",EDGE,"E5");var subQ9=sQuery(id+"F2.wireOp",EDGE,"E60");var subQ10=sQuery(id+"F2.wireOp",EDGE,"E37");var subQ11=sQuery(id+"F2.wireOp",EDGE,"E62");var subQ12=sQuery(id+"F2.wireOp",EDGE,"E6");var subQ13=sQuery(id+"F2.wireOp",EDGE,"E9");var subQ14=sQuery(id+"F2.wireOp",EDGE,"E123");var subQ15=sQuery(id+"F2.wireOp",EDGE,"E122");Q5=makeQuery(id+"F5.boolean.opBoolean","SPLIT",FACE,{"disambiguationData":[TD([makeQuery(id+"F3.boolean.opBoolean","COPY",FACE,{"derivedFrom":makeQuery(id+"F3.opExtrude","SWEPT_FACE",FACE,{"disambiguationData":[OSD([subQ8])]})})])],"derivedFrom":makeQuery(id+"F3.boolean.opBoolean","COPY",FACE,{"derivedFrom":makeQuery(id+"F3.opExtrude","CAP_FACE",FACE,{"disambiguationData":[OSD([subQ8,subQ12,subQ6,subQ13,subQ7,subQ4,subQ5,subQ10,sQuery(id+"F2.wireOp",EDGE,"E38"),subQ1,sQuery(id+"F2.wireOp",EDGE,"E40"),subQ0,subQ9,subQ11,sQuery(id+"F2.wireOp",EDGE,"E63"),subQ3,subQ15,subQ14])],"isStart":false})})});}
            var Q6;
            Q6=makeQuery(id+"F3.boolean.opBoolean","COPY",FACE,{"derivedFrom":makeQuery(id+"F3.opExtrude","CAP_FACE",FACE,{"disambiguationData":[OSD([sQuery(id+"F2.wireOp",EDGE,"E4"),sQuery(id+"F2.wireOp",EDGE,"E18"),sQuery(id+"F2.wireOp",EDGE,"E39"),sQuery(id+"F2.wireOp",EDGE,"E51"),sQuery(id+"F2.wireOp",EDGE,"E52"),sQuery(id+"F2.wireOp",EDGE,"E53"),sQuery(id+"F2.wireOp",EDGE,"E106.MirrorCS"),sQuery(id+"F2.wireOp",EDGE,"E107.MirrorCS"),sQuery(id+"F2.wireOp",EDGE,"E108.MirrorCS")])],"isStart":false})});
            extrude(context, id + "F22", {"entities" : qUnion([Q0, Q1, Q2, Q3, Q4, Q5, Q6]), "operationType" : NewBodyOperationType.REMOVE, "oppositeDirection" : true, "depth" : 25 * mm, "offsetDistance" : 25 * mm});
        }
    });
